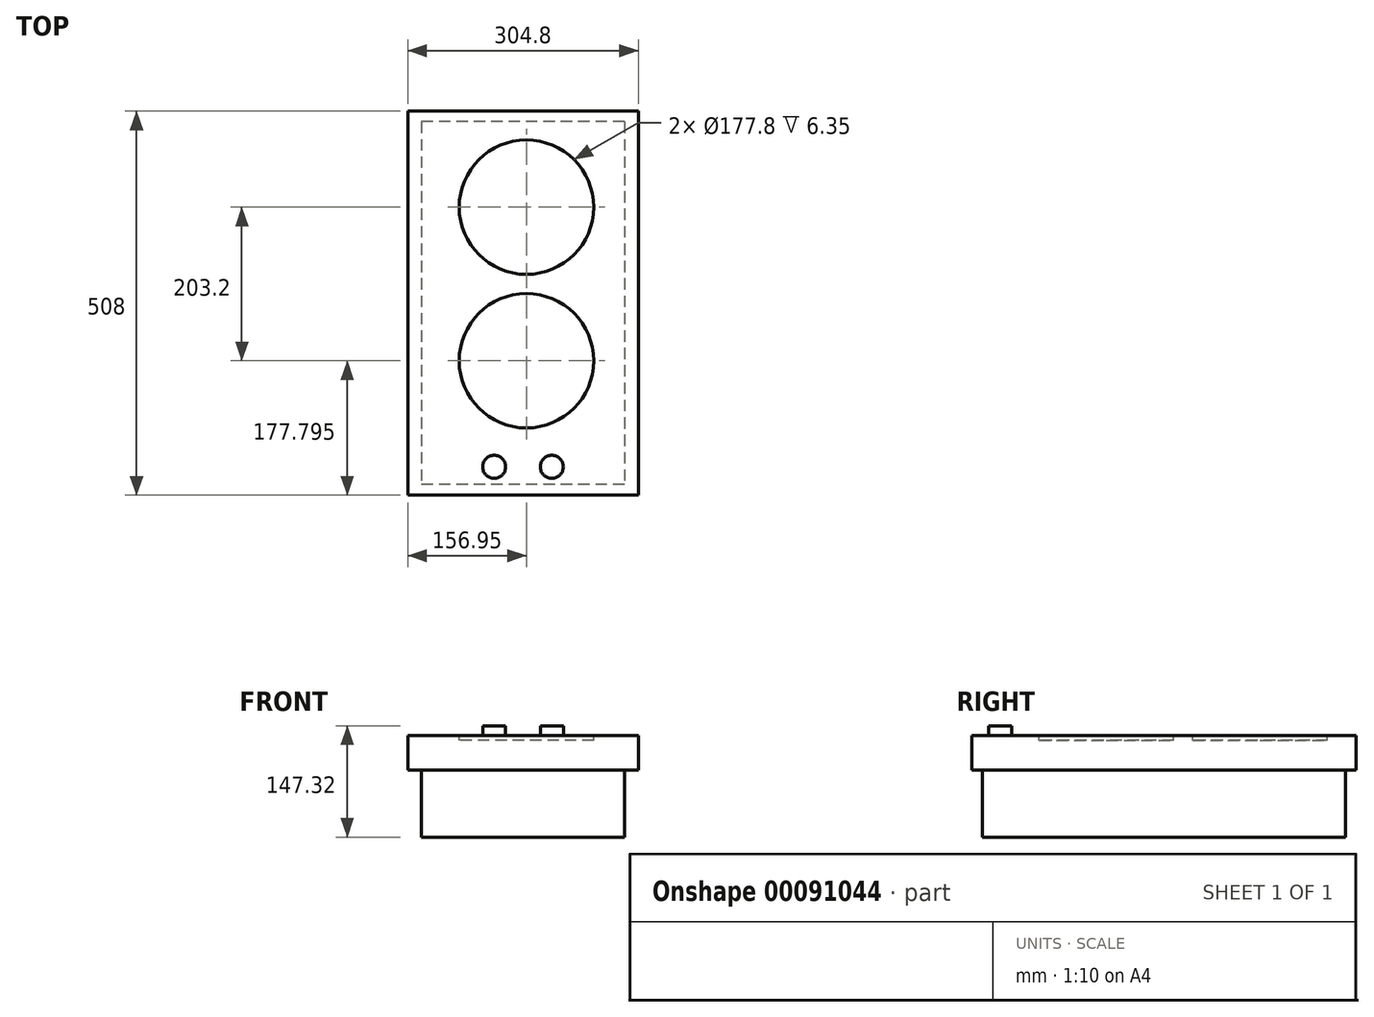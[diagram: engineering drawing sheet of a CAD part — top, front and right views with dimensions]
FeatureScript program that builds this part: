
annotation { "Feature Type Name" : "Feature", "Feature Type Description" : "" }
export const myFeature = defineFeature(function(context is Context, id is Id, definition is map)
    precondition{}
    {
        {
            var Q0;
            Q0=qCreatedBy(makeId("Top.planeOp"),FACE);
            var sketch = newSketch(context, id + "F0", { "sketchPlane" : qUnion([Q0])});
            skLineSegment(sketch, "E0.bottom", {"start": v(-156.95, 284.92) * mm, "end": v(147.85, 284.92) * mm});
            skLineSegment(sketch, "E0.top", {"start": v(-156.95, -223.08) * mm, "end": v(147.85, -223.08) * mm});
            skLineSegment(sketch, "E0.left", {"start": v(-156.95, 284.92) * mm, "end": v(-156.95, -223.08) * mm});
            skLineSegment(sketch, "E0.right", {"start": v(147.85, 284.92) * mm, "end": v(147.85, -223.08) * mm});
            skSolve(sketch);
        }
        {
            var Q0;
            Q0 = qSketchRegion(id + "F0", true);
            extrude(context, id + "F1", {"entities" : qUnion([Q0]), "depth" : 45.72 * mm});
        }
        {
            var Q0;
            Q0=makeQuery(id+"F1.opExtrude","CAP_FACE",FACE,{"disambiguationData":[OSD([sQuery(id+"F0.wireOp",EDGE,"E0.bottom"),sQuery(id+"F0.wireOp",EDGE,"E0.top"),sQuery(id+"F0.wireOp",EDGE,"E0.left"),sQuery(id+"F0.wireOp",EDGE,"E0.right")])],"isStart":true});
            var sketch = newSketch(context, id + "F2", { "sketchPlane" : qUnion([Q0])});
            skLineSegment(sketch, "E1", {"start": v(147.85, -30.92) * mm, "end": v(-156.95, -30.92) * mm, "construction": true});
            skLineSegment(sketch, "E2", {"start": v(-4.55, -284.92) * mm, "end": v(-4.55, 223.08) * mm, "construction": true});
            skPoint(sketch, "E3", {"position": v(-4.55, -30.92) * mm});
            skSolve(sketch);
        }
        {
            var Q0;
            Q0=makeQuery(id+"F1.opExtrude","CAP_FACE",FACE,{"disambiguationData":[OSD([sQuery(id+"F0.wireOp",EDGE,"E0.bottom"),sQuery(id+"F0.wireOp",EDGE,"E0.top"),sQuery(id+"F0.wireOp",EDGE,"E0.left"),sQuery(id+"F0.wireOp",EDGE,"E0.right")])],"isStart":true});
            var sketch = newSketch(context, id + "F3", { "sketchPlane" : qUnion([Q0])});
            skLineSegment(sketch, "E4.bottom", {"start": v(129.43, -270.95) * mm, "end": v(-138.54, -270.95) * mm});
            skLineSegment(sketch, "E4.top", {"start": v(129.43, 209.11) * mm, "end": v(-138.54, 209.11) * mm});
            skLineSegment(sketch, "E4.left", {"start": v(129.43, -270.95) * mm, "end": v(129.43, 209.11) * mm});
            skLineSegment(sketch, "E4.right", {"start": v(-138.54, -270.95) * mm, "end": v(-138.54, 209.11) * mm});
            skPoint(sketch, "E4.middle", {"position": v(-4.55, -30.92) * mm});
            skSolve(sketch);
        }
        {
            var Q0;
            Q0 = qSketchRegion(id + "F3", true);
            extrude(context, id + "F4", {"entities" : qUnion([Q0]), "operationType" : NewBodyOperationType.ADD, "depth" : 88.9 * mm});
        }
        {
            var Q0;
            Q0=makeQuery(id+"F1.opExtrude","CAP_FACE",FACE,{"disambiguationData":[OSD([sQuery(id+"F0.wireOp",EDGE,"E0.bottom"),sQuery(id+"F0.wireOp",EDGE,"E0.top"),sQuery(id+"F0.wireOp",EDGE,"E0.left"),sQuery(id+"F0.wireOp",EDGE,"E0.right")])],"isStart":false});
            var sketch = newSketch(context, id + "F5", { "sketchPlane" : qUnion([Q0])});
            skCircle(sketch, "E5", {"center": v(0, 157.92) * mm, "radius": 88.9 * mm});
            skCircle(sketch, "E6", {"center": v(0, -45.28) * mm, "radius": 88.9 * mm});
            skSolve(sketch);
        }
        {
            var Q0;
            Q0 = qSketchRegion(id + "F5", true);
            extrude(context, id + "F6", {"entities" : qUnion([Q0]), "operationType" : NewBodyOperationType.REMOVE, "oppositeDirection" : true, "depth" : 6.35 * mm});
        }
        {
            var Q0;
            Q0=makeQuery(id+"F1.opExtrude","CAP_FACE",FACE,{"disambiguationData":[OSD([sQuery(id+"F0.wireOp",EDGE,"E0.bottom"),sQuery(id+"F0.wireOp",EDGE,"E0.top"),sQuery(id+"F0.wireOp",EDGE,"E0.left"),sQuery(id+"F0.wireOp",EDGE,"E0.right")])],"isStart":false});
            var sketch = newSketch(context, id + "F7", { "sketchPlane" : qUnion([Q0])});
            skCircle(sketch, "E7", {"center": v(-42.65, -185.57) * mm, "radius": 15.24 * mm});
            skCircle(sketch, "E8", {"center": v(33.55, -185.57) * mm, "radius": 15.24 * mm});
            skSolve(sketch);
        }
        {
            var Q0;
            Q0 = qSketchRegion(id + "F7", true);
            extrude(context, id + "F8", {"entities" : qUnion([Q0]), "operationType" : NewBodyOperationType.ADD, "depth" : 12.7 * mm});
        }
    });
